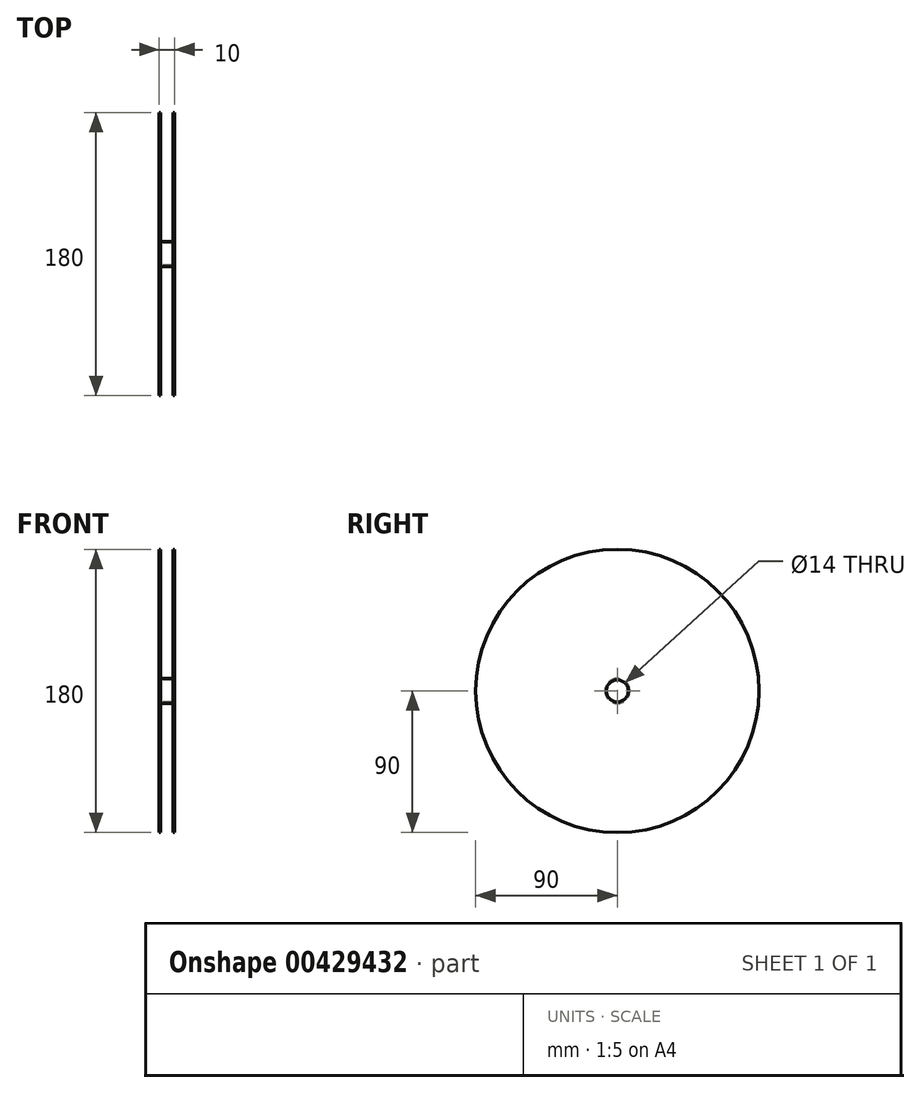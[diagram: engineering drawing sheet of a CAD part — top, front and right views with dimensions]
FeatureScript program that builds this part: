
annotation { "Feature Type Name" : "Feature", "Feature Type Description" : "" }
export const myFeature = defineFeature(function(context is Context, id is Id, definition is map)
    precondition{}
    {
        {
            var Q0;
            Q0=qCreatedBy(makeId("Right.planeOp"),FACE);
            var sketch = newSketch(context, id + "F0", { "sketchPlane" : qUnion([Q0])});
            skCircle(sketch, "E0", {"center": v(0, 0) * mm, "radius": 90 * mm});
            skCircle(sketch, "E1", {"center": v(0, 0) * mm, "radius": 7 * mm});
            skSolve(sketch);
        }
        {
            var Q0;
            Q0=makeQuery(id+"F0.imprint","IMPRINT",FACE,{"disambiguationData":[TD([[makeQuery(id+"F0.imprint","IMPRINT",EDGE,{"derivedFrom":sQuery(id+"F0.wireOp",EDGE,"E0")}),1.0]])]});
            extrude(context, id + "F1", {"entities" : qUnion([Q0]), "depth" : 1 * mm});
        }
        {
            var Q0;
            Q0=makeQuery(id+"F1.opExtrude","CAP_FACE",FACE,{"disambiguationData":[OSD([sQuery(id+"F0.wireOp",EDGE,"E0"),sQuery(id+"F0.wireOp",EDGE,"E1")])],"isStart":false});
            var sketch = newSketch(context, id + "F2", { "sketchPlane" : qUnion([Q0])});
            skCircle(sketch, "E2.0", {"center": v(0, 0) * mm, "radius": 7 * mm});
            skCircle(sketch, "E3", {"center": v(0, 0) * mm, "radius": 8 * mm});
            skSolve(sketch);
        }
        {
            var Q0;
            Q0=makeQuery(id+"F2.imprint","IMPRINT",FACE,{"disambiguationData":[TD([[makeQuery(id+"F2.imprint","IMPRINT",EDGE,{"derivedFrom":sQuery(id+"F2.wireOp",EDGE,"E2.0")}),-1.0]])]});
            extrude(context, id + "F3", {"entities" : qUnion([Q0]), "operationType" : NewBodyOperationType.ADD, "depth" : 8 * mm});
        }
        {
            var Q0;
            Q0=makeQuery(id+"F3.opExtrude","CAP_FACE",FACE,{"disambiguationData":[OSD([sQuery(id+"F2.wireOp",EDGE,"E2.0"),sQuery(id+"F2.wireOp",EDGE,"E3")])],"isStart":false});
            var sketch = newSketch(context, id + "F4", { "sketchPlane" : qUnion([Q0])});
            skCircle(sketch, "E4.0.0", {"center": v(0, 0) * mm, "radius": 90 * mm});
            skSolve(sketch);
        }
        {
            var Q0;
            Q0=makeQuery(id+"F4.imprint","IMPRINT",FACE,{"disambiguationData":[TD([[makeQuery(id+"F4.imprint","IMPRINT",EDGE,{"derivedFrom":sQuery(id+"F4.wireOp",EDGE,"E4.0.0")}),1.0]])]});
            var Q1;
            Q1=makeQuery(id+"F4.imprint","IMPRINT",FACE,{"disambiguationData":[TD([[makeQuery(id+"F4.imprint","IMPRINT",EDGE,{"derivedFrom":makeQuery(id+"F3.opExtrude","CAP_EDGE",EDGE,{"disambiguationData":[OSD([sQuery(id+"F2.wireOp",EDGE,"E2.0")])],"isStart":false})}),-1.0]])]});
            extrude(context, id + "F5", {"entities" : qUnion([Q0, Q1]), "operationType" : NewBodyOperationType.ADD, "depth" : 1 * mm});
        }
    });
